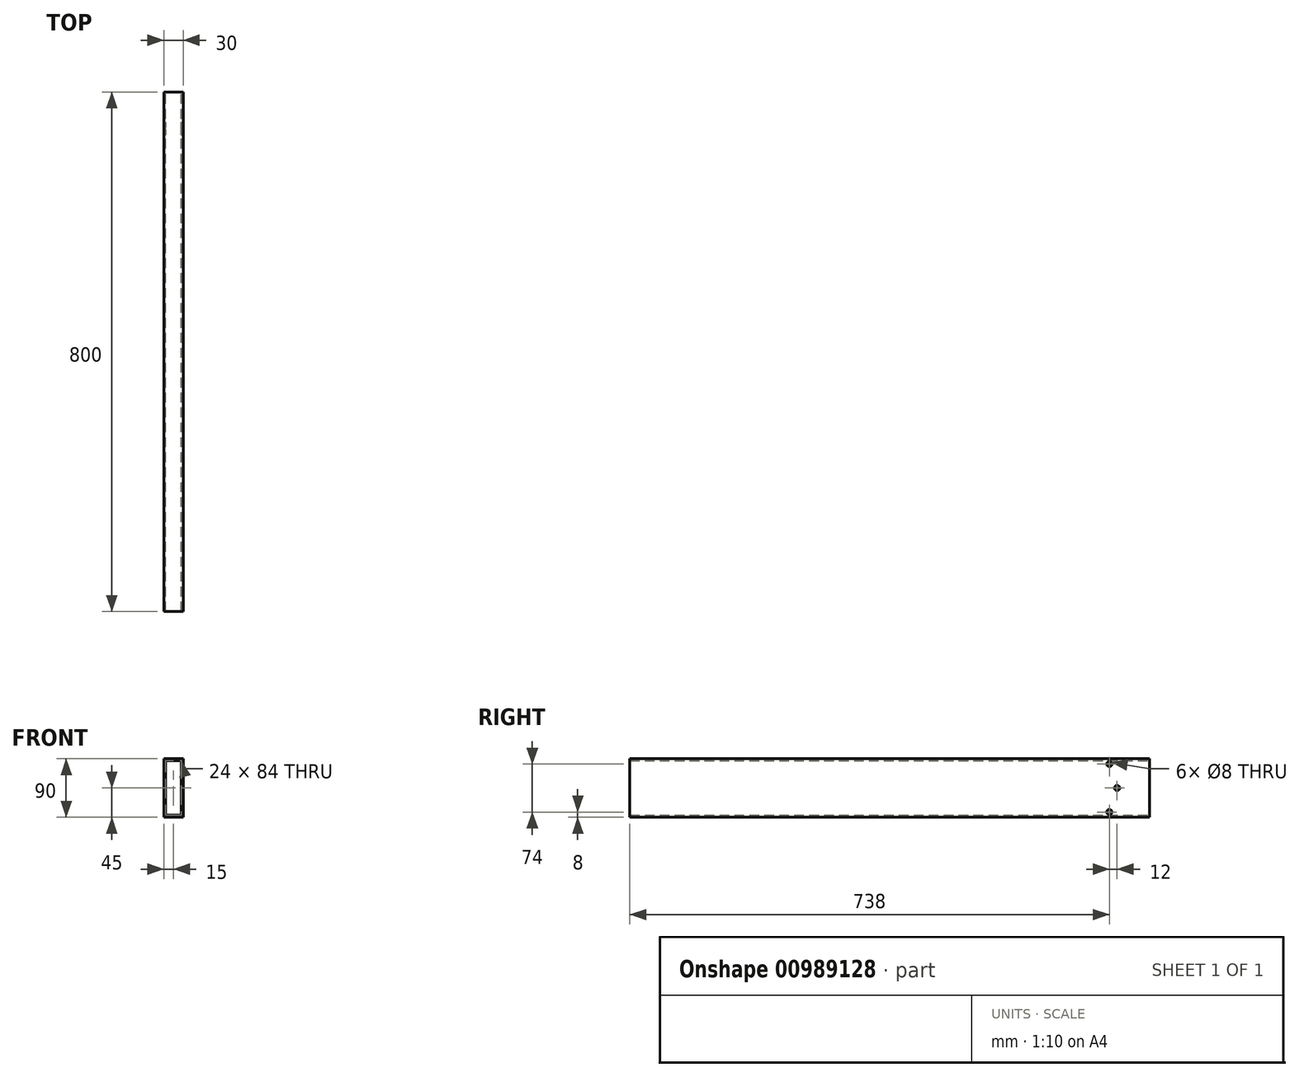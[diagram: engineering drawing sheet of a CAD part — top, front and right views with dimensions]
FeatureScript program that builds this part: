
annotation { "Feature Type Name" : "Feature", "Feature Type Description" : "" }
export const myFeature = defineFeature(function(context is Context, id is Id, definition is map)
    precondition{}
    {
        {
            var Q0;
            Q0=qCreatedBy(makeId("Front.planeOp"),FACE);
            var sketch = newSketch(context, id + "F0", { "sketchPlane" : qUnion([Q0])});
            skLineSegment(sketch, "E0.bottom", {"start": v(15, 45) * mm, "end": v(-15, 45) * mm});
            skLineSegment(sketch, "E0.top", {"start": v(15, -45) * mm, "end": v(-15, -45) * mm});
            skLineSegment(sketch, "E0.left", {"start": v(15, 45) * mm, "end": v(15, -45) * mm});
            skLineSegment(sketch, "E0.right", {"start": v(-15, 45) * mm, "end": v(-15, -45) * mm});
            skPoint(sketch, "E0.middle", {"position": v(0, 0) * mm});
            skSolve(sketch);
        }
        {
            var Q0;
            Q0 = qSketchRegion(id + "F0", true);
            extrude(context, id + "F1", {"entities" : qUnion([Q0]), "endBound" : BoundingType.SYMMETRIC, "depth" : 800 * mm, "offsetDistance" : 25.4 * mm});
        }
        {
            var Q0;
            Q0=makeQuery(id+"F1.opExtrude","CAP_FACE",FACE,{"disambiguationData":[OSD([sQuery(id+"F0.wireOp",EDGE,"E0.bottom"),sQuery(id+"F0.wireOp",EDGE,"E0.top"),sQuery(id+"F0.wireOp",EDGE,"E0.left"),sQuery(id+"F0.wireOp",EDGE,"E0.right")])],"isStart":false});
            var Q1;
            Q1=makeQuery(id+"F1.opExtrude","CAP_FACE",FACE,{"disambiguationData":[OSD([sQuery(id+"F0.wireOp",EDGE,"E0.bottom"),sQuery(id+"F0.wireOp",EDGE,"E0.top"),sQuery(id+"F0.wireOp",EDGE,"E0.left"),sQuery(id+"F0.wireOp",EDGE,"E0.right")])],"isStart":true});
            shell(context, id + "F2", {"entities" : qUnion([Q0, Q1]), "thickness" : 3 * mm});
        }
        {
            var Q0;
            Q0=makeQuery(id+"F1.opExtrude","SWEPT_FACE",FACE,{"disambiguationData":[OSD([sQuery(id+"F0.wireOp",EDGE,"E0.left")])]});
            var sketch = newSketch(context, id + "F3", { "sketchPlane" : qUnion([Q0])});
            skLineSegment(sketch, "E1", {"start": v(0, 0) * mm, "end": v(370, 0) * mm, "construction": true});
            skCircle(sketch, "E2", {"center": v(338, 37) * mm, "radius": 4 * mm});
            skCircle(sketch, "E3", {"center": v(350, 0) * mm, "radius": 4 * mm});
            skCircle(sketch, "E4", {"center": v(338, -37) * mm, "radius": 4 * mm});
            skSolve(sketch);
        }
        {
            var Q0;
            Q0 = qSketchRegion(id + "F3", true);
            extrude(context, id + "F4", {"entities" : qUnion([Q0]), "operationType" : NewBodyOperationType.REMOVE, "endBound" : BoundingType.THROUGH_ALL, "oppositeDirection" : true, "depth" : 25 * mm, "offsetDistance" : 25 * mm});
        }
    });
